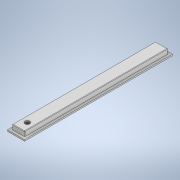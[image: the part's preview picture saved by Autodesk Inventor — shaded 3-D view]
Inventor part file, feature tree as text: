
AUTODESK INVENTOR PART (.ipt)
format: ipt  version: 2020 (Build 240168000, 168)  size: 131,584 bytes
history: native  units: mm
features: extrude x3, sketch x3, projected_geometry x2, fillet x1
ambient origin geometry x8: Origin, YZ Plane, XZ Plane, XY Plane, X Axis, Y Axis, Z Axis, Center Point
bodies: Solid1 (feature_tree)
feature tree (9):
  extrude  "Extrusion1"  Depth=297.0mm
  extrude  "Extrusion2"  Depth=5.0mm
  extrude  "Extrusion3"  Depth=10.0mm
  fillet  "Fillet1"  Radius=130.0mm
  sketch  "Sketch1"  dims[d0=25.4mm d1=297.0mm]
  sketch  "Sketch2"  dims[d2=10.0mm d3=0.0mm d4=5.0mm]
  projected_geometry  "Projected Loop1"
  sketch  "Sketch3"  dims[d5=3.0mm d6=0.0mm d7=10.0mm d8=130.0mm d9=0.0mm d10=0.0mm d11=1.0mm]
  projected_geometry  "Projected Loop2"
